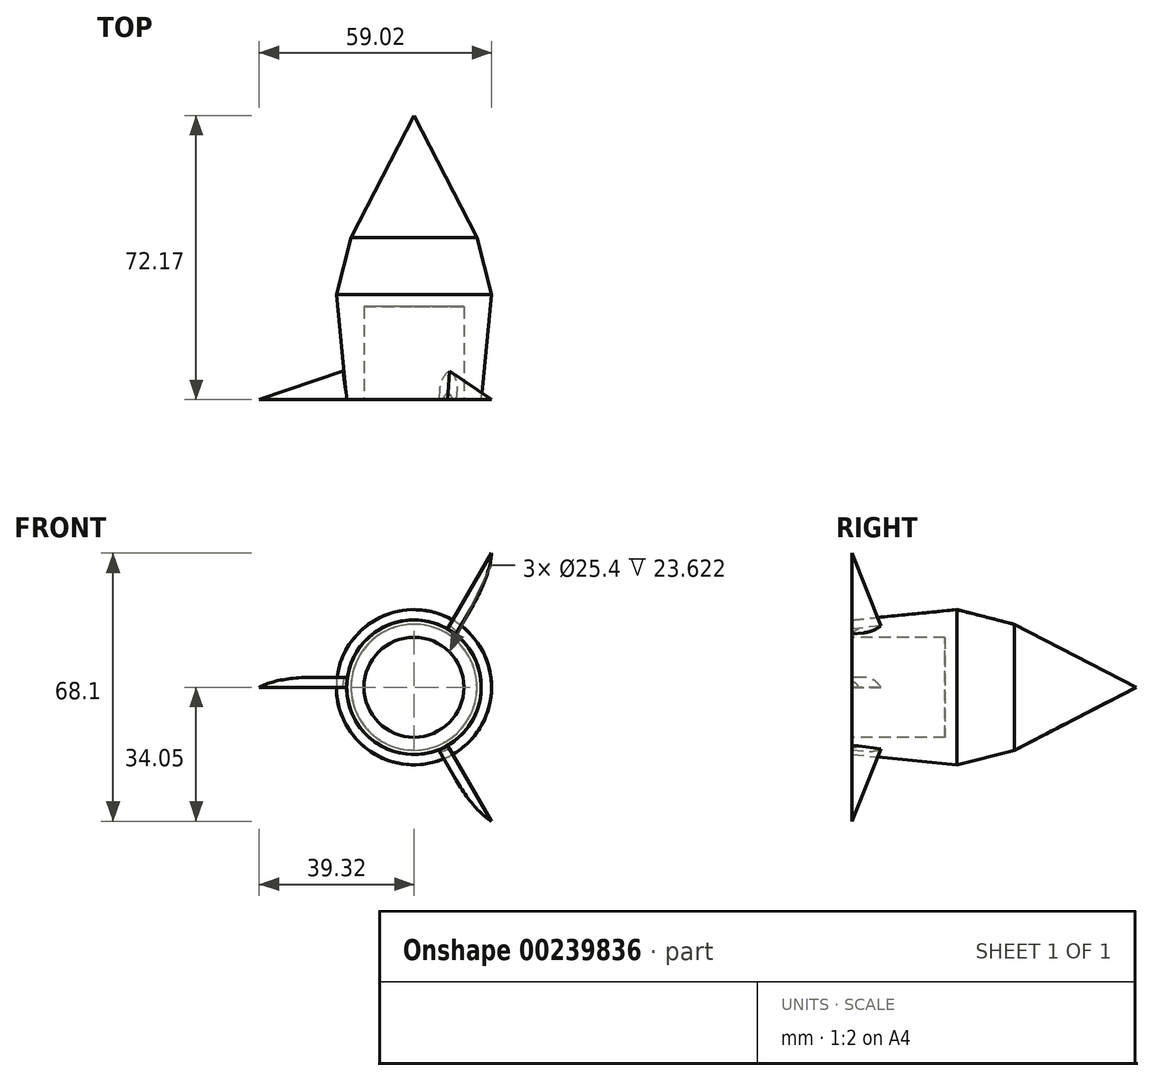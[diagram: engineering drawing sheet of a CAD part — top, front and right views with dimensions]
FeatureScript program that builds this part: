
annotation { "Feature Type Name" : "Feature", "Feature Type Description" : "" }
export const myFeature = defineFeature(function(context is Context, id is Id, definition is map)
    precondition{}
    {
        {
            var Q0;
            Q0=qCreatedBy(makeId("Top.planeOp"),FACE);
            var sketch = newSketch(context, id + "F0", { "sketchPlane" : qUnion([Q0])});
            skLineSegment(sketch, "E0", {"start": v(0, 0) * mm, "end": v(-17.1, 0) * mm});
            skLineSegment(sketch, "E1", {"start": v(-17.1, 0) * mm, "end": v(-19.7, 26.67) * mm});
            skLineSegment(sketch, "E2", {"start": v(-19.7, 26.67) * mm, "end": v(-16, 41.26) * mm});
            skLineSegment(sketch, "E3", {"start": v(-16, 41.26) * mm, "end": v(0, 72.17) * mm});
            skLineSegment(sketch, "E4", {"start": v(0, 72.17) * mm, "end": v(0, 45.83) * mm});
            skLineSegment(sketch, "E5", {"start": v(0, 45.83) * mm, "end": v(0, 0) * mm});
            skSolve(sketch);
        }
        {
            var Q0;
            Q0=makeQuery(id+"F0.imprint","IMPRINT",FACE,{"disambiguationData":[TD([[makeQuery(id+"F0.imprint","IMPRINT",EDGE,{"derivedFrom":sQuery(id+"F0.wireOp",EDGE,"E0")}),-1.0]])]});
            var Q1;
            Q1=sQuery(id+"F0.wireOp",EDGE,"E5");
            revolve(context, id + "F1", {"entities" : qUnion([Q0]), "axis" : qUnion([Q1]), "revolveType" : RevolveType.FULL});
        }
        {
            var Q0;
            Q0=qCreatedBy(makeId("Front.planeOp"),FACE);
            var sketch = newSketch(context, id + "F2", { "sketchPlane" : qUnion([Q0])});
            skCircle(sketch, "E6", {"center": v(0, 0) * mm, "radius": 12.7 * mm});
            skSolve(sketch);
        }
        {
            var Q0;
            Q0 = qSketchRegion(id + "F2", true);
            extrude(context, id + "F3", {"entities" : qUnion([Q0]), "operationType" : NewBodyOperationType.REMOVE, "oppositeDirection" : true, "depth" : 23.62 * mm});
        }
        {
            var Q0;
            Q0=qCreatedBy(makeId("Top.planeOp"),FACE);
            var sketch = newSketch(context, id + "F4", { "sketchPlane" : qUnion([Q0])});
            skLineSegment(sketch, "E7", {"start": v(-17.03, 0) * mm, "end": v(-39.32, 0) * mm});
            skLineSegment(sketch, "E8", {"start": v(-39.32, 0) * mm, "end": v(-18.04, 7.29) * mm});
            skLineSegment(sketch, "E9", {"start": v(-18.04, 7.29) * mm, "end": v(-17.03, 0) * mm});
            skSolve(sketch);
        }
        {
            var Q0;
            Q0=makeQuery(id+"F4.imprint","IMPRINT",FACE,{"disambiguationData":[TD([[makeQuery(id+"F4.imprint","IMPRINT",EDGE,{"derivedFrom":sQuery(id+"F4.wireOp",EDGE,"E7")}),-1.0]])]});
            extrude(context, id + "F5", {"entities" : qUnion([Q0]), "operationType" : NewBodyOperationType.ADD, "depth" : 2.54 * mm});
        }
        {
            var Q0;
            Q0=makeQuery(id+"F5.opExtrude","CAP_EDGE",EDGE,{"disambiguationData":[OSD([sQuery(id+"F4.wireOp",EDGE,"E8")])],"isStart":false});
            fillet(context, id + "F6", {"entities" : qUnion([Q0]), "radius" : 5.08 * mm, "tangentPropagation" : true, "allowEdgeOverflow" : false});
        }
        {
            var Q0;
            Q0=makeQuery(id+"F1.opRevolve","SWEPT_BODY",BODY,{"disambiguationData":[OSD([sQuery(id+"F0.wireOp",EDGE,"E0"),sQuery(id+"F0.wireOp",EDGE,"E1"),sQuery(id+"F0.wireOp",EDGE,"E2"),sQuery(id+"F0.wireOp",EDGE,"E3"),sQuery(id+"F0.wireOp",EDGE,"E4"),sQuery(id+"F0.wireOp",EDGE,"E5")])]});
            var Q1;
            Q1=makeQuery(id+"F1.opRevolve","SWEPT_EDGE",EDGE,{"disambiguationData":[OSD([sQuery(id+"F0.wireOp",EDGE,"E1"),sQuery(id+"F0.wireOp",EDGE,"E2")])]});
            circularPattern(context, id + "F7", {"entities" : qUnion([Q0]), "axis" : qUnion([Q1]), "angle" : 360 * degree, "instanceCount" : 3, "equalSpace" : true});
        }
    });
